# Revit family: QF_COO_SKFMSD4011D-MB_DEU
name_source: partatom
category: Sonderausstattung
revit_build: Autodesk Revit 2018 (Build: 20180423_1000(x64)
units: mm (PartAtom-declared; Revit-internal decimal feet)

## family parameters
Arbeitsebenenbasiert = Nein
Beim Laden mit Abzugskörper schneiden = Nein
Bemaßung runder Anschluss = Durchmesser verwenden
Gemeinsam genutzt = Nein
Immer vertikal = Ja
OmniClass-Nummer = 23.40.40.00
OmniClass-Titel = Food Service Equipment and Furnishings
Raumberechnungspunkt = Nein
Teiletyp = Normal

## types (1)
- SKFMSD4011D-MB
    Anlaufstrom = 28 A
    Anschlusshöhe FFB = 2338 mm
    Anschlusshöhe RFB = 0 mm  [stored 0 ft]
    Artikel Nummer = SKFMSD2011D-MB
    Beschreibung = Schnellkühler / Schockfroster
    Beschreibung durch Hersteller analog Leistungsverzeichniskurztext = Schnellkühler / Schockfroster, Kombi-Gerät, Durchfahrgerät, Eigenkühlung für Kältemittel R452a
    Beschreibung durch Hersteller analog Leistungsverzeichnislangtext = Schnellkühler / Schockfroster, Kombi-Gerät, Durchfahrgerät, Eigenkühlung für Kältemittel R452a
    Betriebsstrom = 28 A
    CE Kennzeichnung = Ja
    Elektrische leistung = 13200 W
    Ersteller = Cool Compact Kühlgeräte GmbH
    Fließstrom = 22 A
    Gerätegewicht Netto = 610.00 kg
    Großküchengerätezuordnung = Ja
    Hersteller = Cool Compact Kühlgeräte GmbH
    Höhe = 2433 mm
    Internetadresse Gerätehersteller = www.coolcompact.de
    Internetadresse für Ersatzteilliste = www.coolcompact.de
    Internetadresse für die Maßzeichnung = www.coolcompact.de
    Internetadresse für kritische Ersatzteilliste = www.coolcompact.de
    Kondensat Leitung = 40 mm
    Kondensat Leitung Anschlusshöhe FFB = 339 mm
    Kondensat Leitung Anschlusshöhe RFB = 0 mm  [stored 0 ft]
    Kälte Abmessung Flüssigkeitsleitung = 0 mm  [stored 0 ft]
    Kälte Abmessung Saugleitung = 0 mm  [stored 0 ft]
    Kälte Betriebsdruck = 18.0 bar
    Kälte Externer Kompressor = Ja
    Kälte Tauwasserablauf = Ja
    Kälte Verdampfungstemperatur = -10 °C
    Kälteleistung = 24000 W
    Kältemittel = R452a
    Kältemittelmenge = 0
    Länge Gerätebreite = 1550 mm
    Maximale Geräteabsicherung = 32 A
    Menge als Set = Ja
    Minimale Stromaufnahme = 11 A
    Modell = SKFMSD2011D-MB
    Phasen = 0
    Produktionsjahr = 2022
    Schalldruckpegel = 46 dBA in 10 meter
    Siphon am Gerät = Ja
    Spannung = 380 V
    Stecker System = -
    Tiefe = 1545 mm
    URL = www.coolcompact.de
    Zubehör = Ja
    Zuleitung zum Gerät im Lieferumfang = Nein

note: [stored X ft] marks values corroborated as IEEE doubles in the binary element streams (Revit-internal decimal feet)
